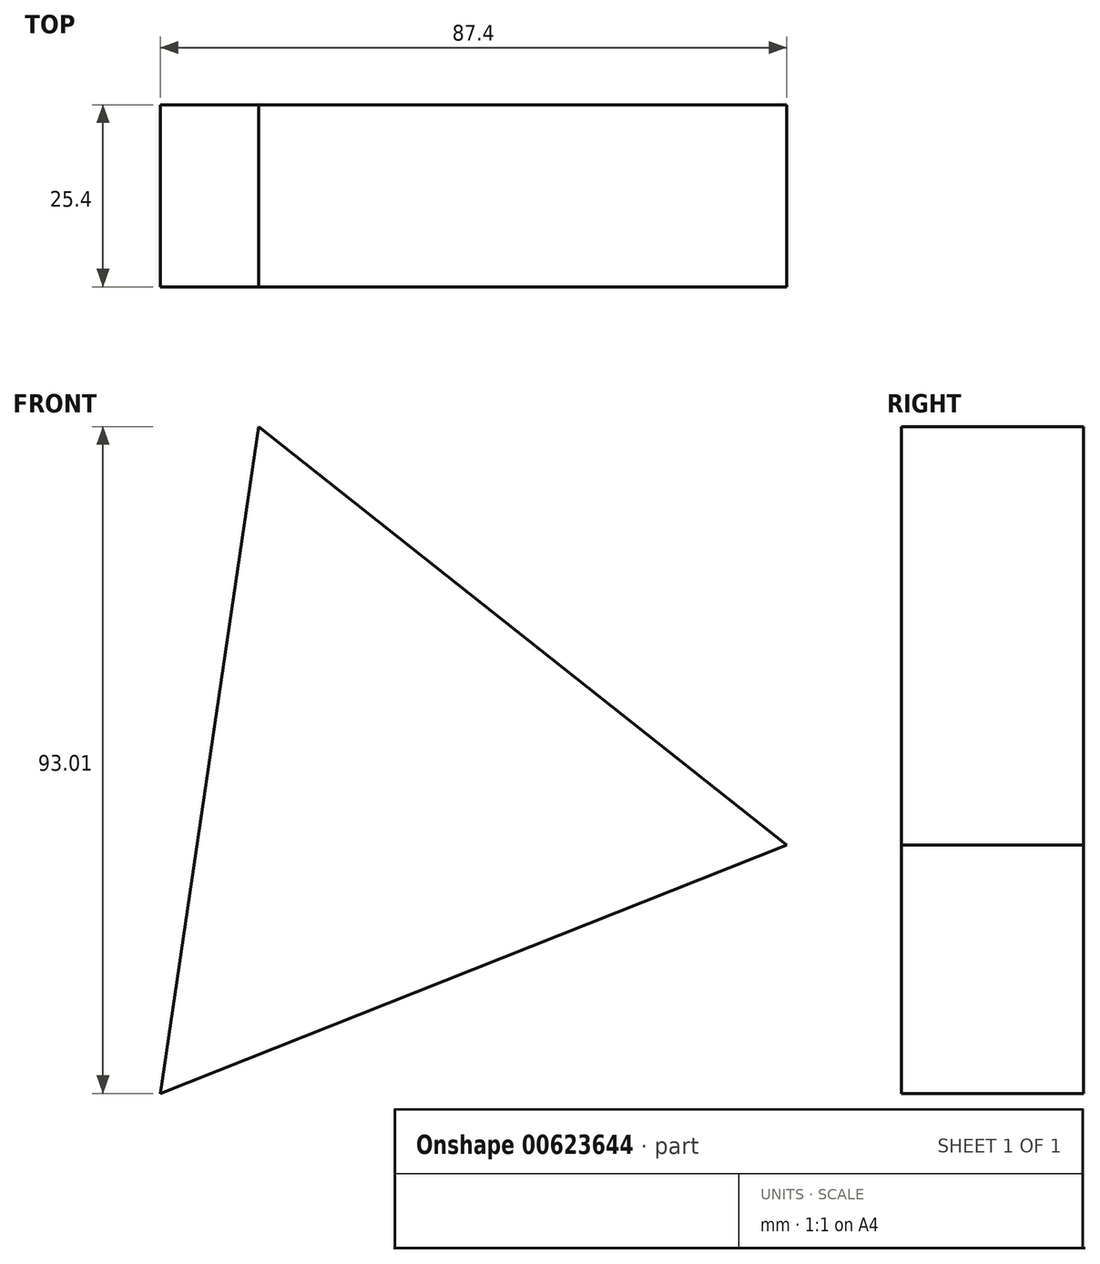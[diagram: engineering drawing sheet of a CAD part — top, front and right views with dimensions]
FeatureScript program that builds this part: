
annotation { "Feature Type Name" : "Feature", "Feature Type Description" : "" }
export const myFeature = defineFeature(function(context is Context, id is Id, definition is map)
    precondition{}
    {
        {
            var Q0;
            Q0=qCreatedBy(makeId("Front.planeOp"),FACE);
            var sketch = newSketch(context, id + "F0", { "sketchPlane" : qUnion([Q0])});
            skCircle(sketch, "E0.cCircle", {"center": v(0, 0) * mm, "radius": 27.14 * mm, "construction": true});
            skLineSegment(sketch, "E0.0", {"start": v(-20, 50.46) * mm, "end": v(53.7, -7.9) * mm});
            skLineSegment(sketch, "E0.1", {"start": v(53.7, -7.9) * mm, "end": v(-33.7, -42.55) * mm});
            skLineSegment(sketch, "E0.2", {"start": v(-33.7, -42.55) * mm, "end": v(-20, 50.46) * mm});
            skPoint(sketch, "E0.0.midPoint", {"position": v(16.85, 21.28) * mm});
            skSolve(sketch);
        }
        {
            var Q0;
            Q0=makeQuery(id+"F0.imprint","IMPRINT",FACE,{"disambiguationData":[TD([[makeQuery(id+"F0.imprint","IMPRINT",EDGE,{"derivedFrom":sQuery(id+"F0.wireOp",EDGE,"E0.0")}),-1.0]])]});
            extrude(context, id + "F1", {"entities" : qUnion([Q0]), "depth" : 25.4 * mm, "offsetDistance" : 25.4 * mm});
        }
    });
